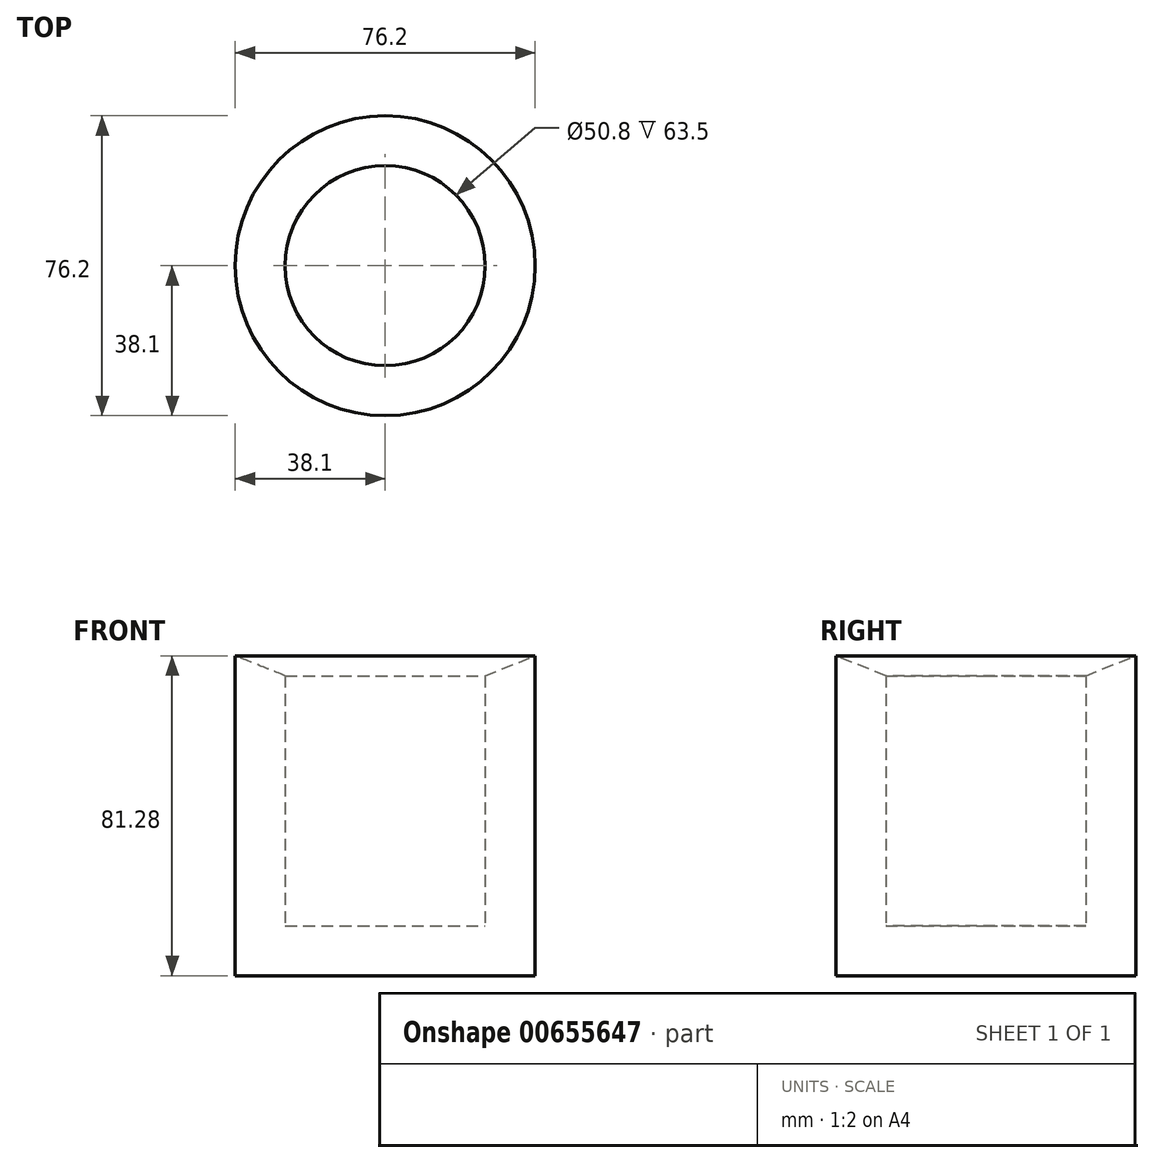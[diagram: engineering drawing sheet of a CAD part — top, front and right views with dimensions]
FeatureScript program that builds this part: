
annotation { "Feature Type Name" : "Feature", "Feature Type Description" : "" }
export const myFeature = defineFeature(function(context is Context, id is Id, definition is map)
    precondition{}
    {
        {
            var Q0;
            Q0=qCreatedBy(makeId("Front.planeOp"),FACE);
            var sketch = newSketch(context, id + "F0", { "sketchPlane" : qUnion([Q0])});
            skLineSegment(sketch, "E0", {"start": v(-38.1, 78.86) * mm, "end": v(-38.1, -2.42) * mm});
            skLineSegment(sketch, "E1", {"start": v(-38.1, -2.42) * mm, "end": v(0, -2.42) * mm});
            skLineSegment(sketch, "E2", {"start": v(0, -2.42) * mm, "end": v(0, 10.28) * mm});
            skLineSegment(sketch, "E3", {"start": v(0, 10.28) * mm, "end": v(-25.4, 10.28) * mm});
            skLineSegment(sketch, "E4", {"start": v(-25.4, 10.28) * mm, "end": v(-25.4, 73.78) * mm});
            skLineSegment(sketch, "E5", {"start": v(-25.4, 73.78) * mm, "end": v(-38.1, 78.86) * mm});
            skSolve(sketch);
        }
        {
            var Q0;
            Q0=makeQuery(id+"F0.imprint","IMPRINT",FACE,{"disambiguationData":[TD([[makeQuery(id+"F0.imprint","IMPRINT",EDGE,{"derivedFrom":sQuery(id+"F0.wireOp",EDGE,"E0")}),1.0]])]});
            var Q1;
            Q1=sQuery(id+"F0.wireOp",EDGE,"E2");
            revolve(context, id + "F1", {"entities" : qUnion([Q0]), "axis" : qUnion([Q1]), "revolveType" : RevolveType.FULL});
        }
    });
